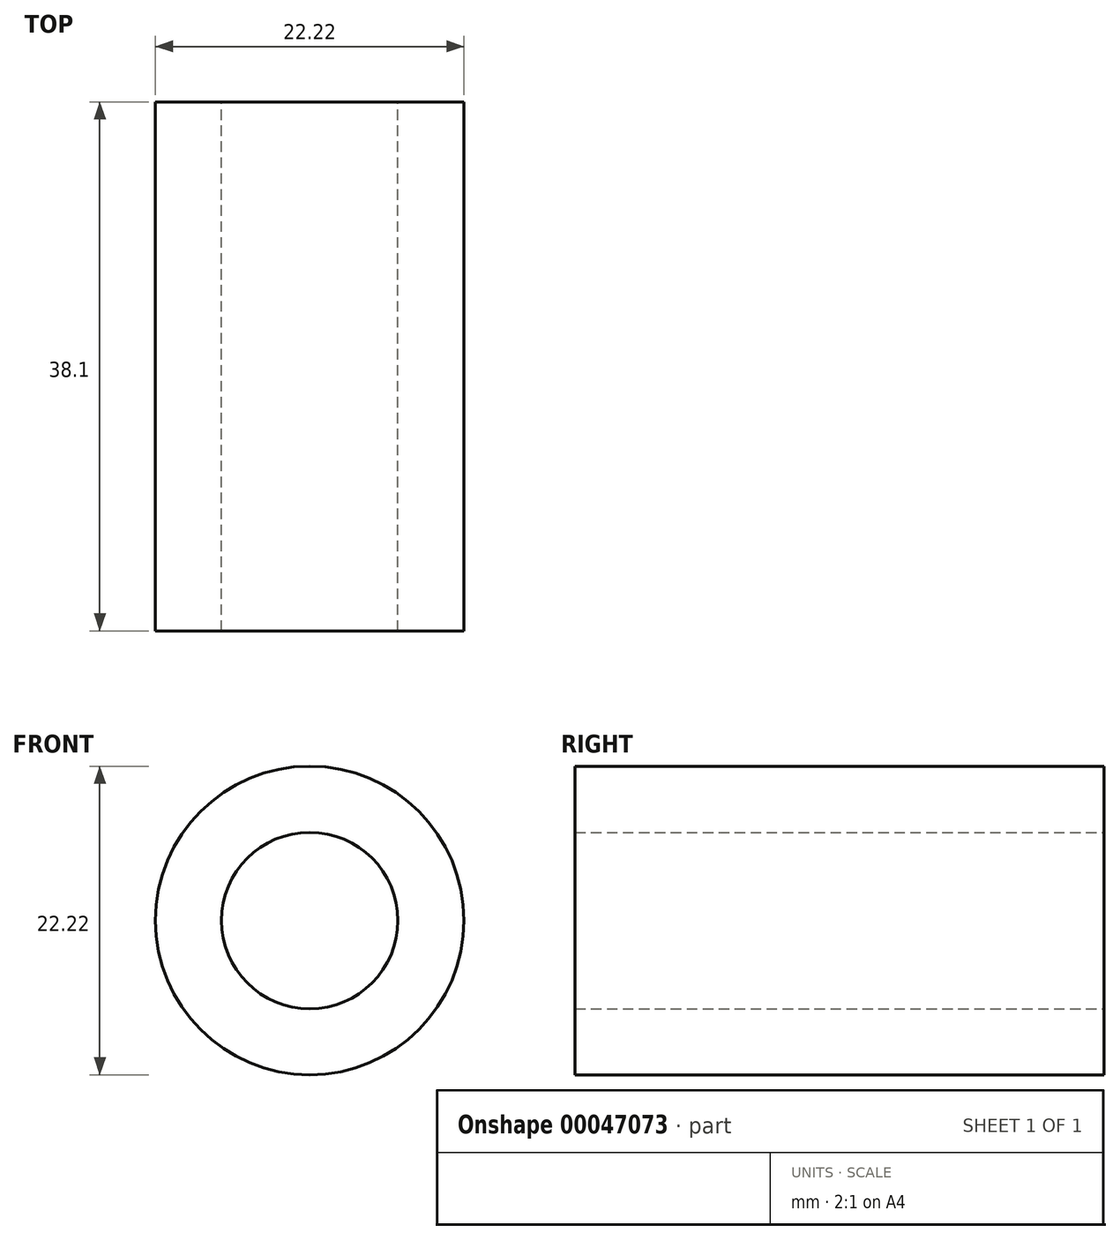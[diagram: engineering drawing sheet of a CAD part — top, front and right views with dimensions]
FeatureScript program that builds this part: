
annotation { "Feature Type Name" : "Feature", "Feature Type Description" : "" }
export const myFeature = defineFeature(function(context is Context, id is Id, definition is map)
    precondition{}
    {
        {
            var Q0;
            Q0=qCreatedBy(makeId("Front.planeOp"),FACE);
            var sketch = newSketch(context, id + "F0", { "sketchPlane" : qUnion([Q0])});
            skCircle(sketch, "E0", {"center": v(0, 0) * mm, "radius": 11.11 * mm});
            skCircle(sketch, "E1", {"center": v(0, 0) * mm, "radius": 6.35 * mm});
            skSolve(sketch);
        }
        {
            var Q0;
            Q0=makeQuery(id+"F0.imprint","IMPRINT",FACE,{"disambiguationData":[TD([[makeQuery(id+"F0.imprint","IMPRINT",EDGE,{"derivedFrom":sQuery(id+"F0.wireOp",EDGE,"E0")}),1.0]])]});
            extrude(context, id + "F1", {"entities" : qUnion([Q0]), "endBound" : BoundingType.SYMMETRIC, "depth" : 38.1 * mm});
        }
    });
